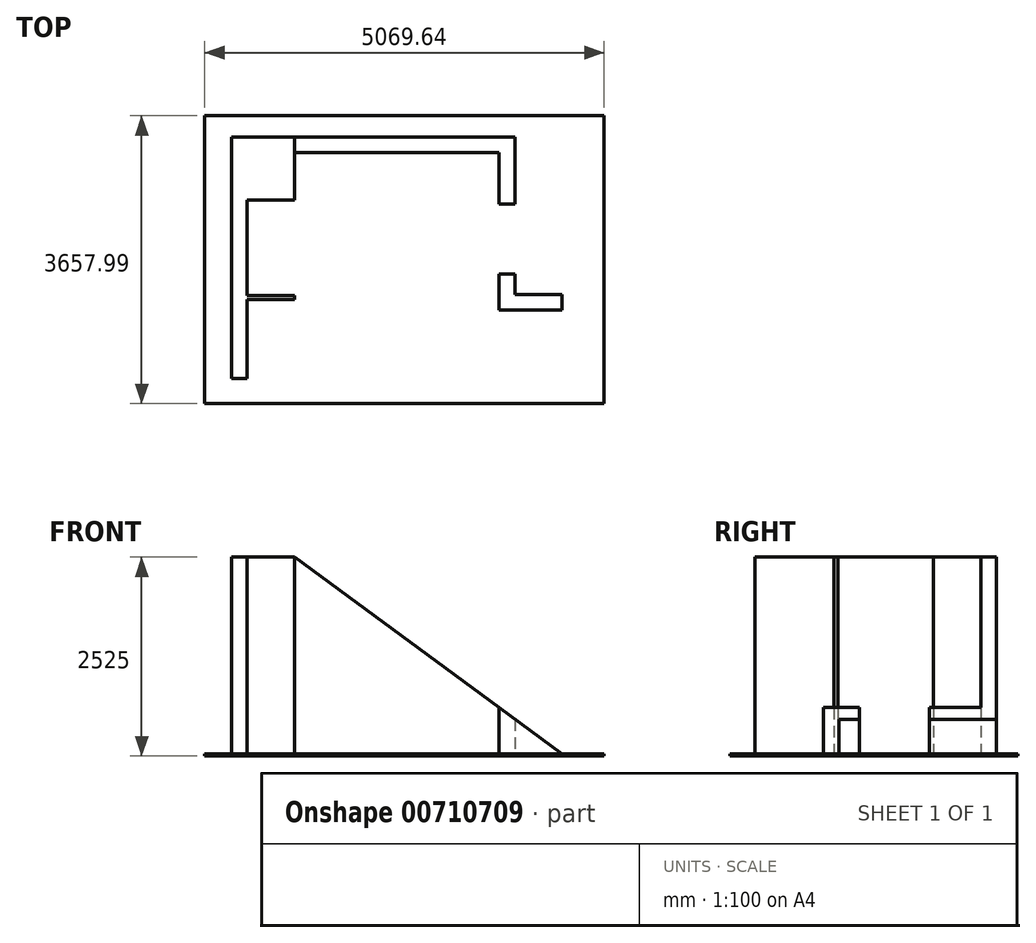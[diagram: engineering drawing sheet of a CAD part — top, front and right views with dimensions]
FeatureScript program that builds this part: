
annotation { "Feature Type Name" : "Feature", "Feature Type Description" : "" }
export const myFeature = defineFeature(function(context is Context, id is Id, definition is map)
    precondition{}
    {
        {
            var Q0;
            Q0=qCreatedBy(makeId("Top.planeOp"),FACE);
            var sketch = newSketch(context, id + "F0", { "sketchPlane" : qUnion([Q0])});
            skLineSegment(sketch, "E0", {"start": v(0, 0) * mm, "end": v(0, 1000) * mm});
            skLineSegment(sketch, "E1", {"start": v(0, 1000) * mm, "end": v(600, 1000) * mm});
            skLineSegment(sketch, "E2", {"start": v(600, 1000) * mm, "end": v(600, 1050) * mm});
            skLineSegment(sketch, "E3", {"start": v(600, 1050) * mm, "end": v(0, 1050) * mm});
            skLineSegment(sketch, "E4", {"start": v(0, 1050) * mm, "end": v(0, 2265) * mm});
            skLineSegment(sketch, "E5", {"start": v(0, 2265) * mm, "end": v(600, 2265) * mm});
            skLineSegment(sketch, "E6", {"start": v(600, 2265) * mm, "end": v(600, 2865) * mm});
            skLineSegment(sketch, "E7", {"start": v(600, 2865) * mm, "end": v(3200, 2865) * mm});
            skLineSegment(sketch, "E8", {"start": v(3200, 2865) * mm, "end": v(3200, 865) * mm});
            skLineSegment(sketch, "E9", {"start": v(3200, 865) * mm, "end": v(4000, 865) * mm});
            skLineSegment(sketch, "E10", {"start": v(4000, 865) * mm, "end": v(4000, 0) * mm});
            skLineSegment(sketch, "E11", {"start": v(4000, 0) * mm, "end": v(0, 0) * mm, "construction": true});
            skLineSegment(sketch, "E12", {"start": v(0, 0) * mm, "end": v(-200, 0) * mm});
            skLineSegment(sketch, "E13", {"start": v(-200, 0) * mm, "end": v(-200, 3065) * mm});
            skLineSegment(sketch, "E14", {"start": v(-200, 3065) * mm, "end": v(3400, 3065) * mm});
            skLineSegment(sketch, "E15", {"start": v(3400, 3065) * mm, "end": v(3400, 1065) * mm});
            skLineSegment(sketch, "E16", {"start": v(3400, 1065) * mm, "end": v(4200, 1065) * mm});
            skLineSegment(sketch, "E17", {"start": v(4200, 1065) * mm, "end": v(4200, 0) * mm});
            skLineSegment(sketch, "E18", {"start": v(4200, 0) * mm, "end": v(4000, 0) * mm});
            skSolve(sketch);
        }
        {
            var Q0;
            Q0=qCreatedBy(makeId("Top.planeOp"),FACE);
            var sketch = newSketch(context, id + "F1", { "sketchPlane" : qUnion([Q0])});
            skLineSegment(sketch, "E19.bottom", {"start": v(-538.18, -321.62) * mm, "end": v(4531.46, -321.62) * mm});
            skLineSegment(sketch, "E19.top", {"start": v(-538.18, 3336.37) * mm, "end": v(4531.46, 3336.37) * mm});
            skLineSegment(sketch, "E19.left", {"start": v(-538.18, -321.62) * mm, "end": v(-538.18, 3336.37) * mm});
            skLineSegment(sketch, "E19.right", {"start": v(4531.46, -321.62) * mm, "end": v(4531.46, 3336.37) * mm});
            skSolve(sketch);
        }
        {
            var Q0;
            Q0 = qSketchRegion(id + "F0", true);
            extrude(context, id + "F2", {"entities" : qUnion([Q0]), "depth" : 2500 * mm, "offsetDistance" : 25 * mm});
        }
        {
            var Q0;
            Q0 = qSketchRegion(id + "F1", true);
            extrude(context, id + "F3", {"entities" : qUnion([Q0]), "operationType" : NewBodyOperationType.ADD, "oppositeDirection" : true, "depth" : 25 * mm, "offsetDistance" : 25 * mm});
        }
        {
            var Q0;
            Q0=makeQuery(id+"F2.opExtrude","CAP_FACE",FACE,{"disambiguationData":[OSD([sQuery(id+"F0.wireOp",EDGE,"E0"),sQuery(id+"F0.wireOp",EDGE,"E1"),sQuery(id+"F0.wireOp",EDGE,"E2"),sQuery(id+"F0.wireOp",EDGE,"E3"),sQuery(id+"F0.wireOp",EDGE,"E4"),sQuery(id+"F0.wireOp",EDGE,"E5"),sQuery(id+"F0.wireOp",EDGE,"E6"),sQuery(id+"F0.wireOp",EDGE,"E7"),sQuery(id+"F0.wireOp",EDGE,"E8"),sQuery(id+"F0.wireOp",EDGE,"E9"),sQuery(id+"F0.wireOp",EDGE,"E10"),sQuery(id+"F0.wireOp",EDGE,"E12"),sQuery(id+"F0.wireOp",EDGE,"E13"),sQuery(id+"F0.wireOp",EDGE,"E14"),sQuery(id+"F0.wireOp",EDGE,"E15"),sQuery(id+"F0.wireOp",EDGE,"E16"),sQuery(id+"F0.wireOp",EDGE,"E17"),sQuery(id+"F0.wireOp",EDGE,"E18")])],"isStart":false});
            var sketch = newSketch(context, id + "F4", { "sketchPlane" : qUnion([Q0])});
            skLineSegment(sketch, "E20.bottom", {"start": v(3200, 2215) * mm, "end": v(3400, 2215) * mm});
            skLineSegment(sketch, "E20.top", {"start": v(3200, 1325) * mm, "end": v(3400, 1325) * mm});
            skLineSegment(sketch, "E20.left", {"start": v(3200, 2215) * mm, "end": v(3200, 1325) * mm});
            skLineSegment(sketch, "E20.right", {"start": v(3400, 2215) * mm, "end": v(3400, 1325) * mm});
            skLineSegment(sketch, "E21.bottom", {"start": v(4000, 1065) * mm, "end": v(4200, 1065) * mm});
            skLineSegment(sketch, "E21.top", {"start": v(4000, 0) * mm, "end": v(4200, 0) * mm});
            skLineSegment(sketch, "E21.left", {"start": v(4000, 1065) * mm, "end": v(4000, 0) * mm});
            skLineSegment(sketch, "E21.right", {"start": v(4200, 1065) * mm, "end": v(4200, 0) * mm});
            skSolve(sketch);
        }
        {
            var Q0;
            Q0 = qSketchRegion(id + "F4", true);
            var Q1;
            Q1=makeQuery(id+"F3.opExtrude","CAP_FACE",FACE,{"disambiguationData":[OSD([sQuery(id+"F1.wireOp",EDGE,"E19.bottom"),sQuery(id+"F1.wireOp",EDGE,"E19.top"),sQuery(id+"F1.wireOp",EDGE,"E19.left"),sQuery(id+"F1.wireOp",EDGE,"E19.right")])],"isStart":true});
            extrude(context, id + "F5", {"entities" : qUnion([Q0]), "operationType" : NewBodyOperationType.REMOVE, "endBound" : BoundingType.UP_TO_SURFACE, "oppositeDirection" : true, "depth" : 25 * mm, "endBoundEntityFace" : qUnion([Q1]), "offsetDistance" : 25 * mm});
        }
        {
            var Q0;
            Q0=makeQuery(id+"F2.opExtrude","SWEPT_FACE",FACE,{"disambiguationData":[OSD([sQuery(id+"F0.wireOp",EDGE,"E12")])]});
            var sketch = newSketch(context, id + "F6", { "sketchPlane" : qUnion([Q0])});
            skLineSegment(sketch, "E22", {"start": v(600, 2500) * mm, "end": v(4000, 0) * mm});
            skLineSegment(sketch, "E23", {"start": v(4000, 0) * mm, "end": v(4000, 2500) * mm});
            skLineSegment(sketch, "E24", {"start": v(4000, 2500) * mm, "end": v(600, 2500) * mm});
            skSolve(sketch);
        }
        {
            var Q0;
            Q0 = qSketchRegion(id + "F6", true);
            extrude(context, id + "F7", {"entities" : qUnion([Q0]), "operationType" : NewBodyOperationType.REMOVE, "endBound" : BoundingType.THROUGH_ALL, "oppositeDirection" : true, "depth" : 25 * mm, "offsetDistance" : 25 * mm});
        }
    });
